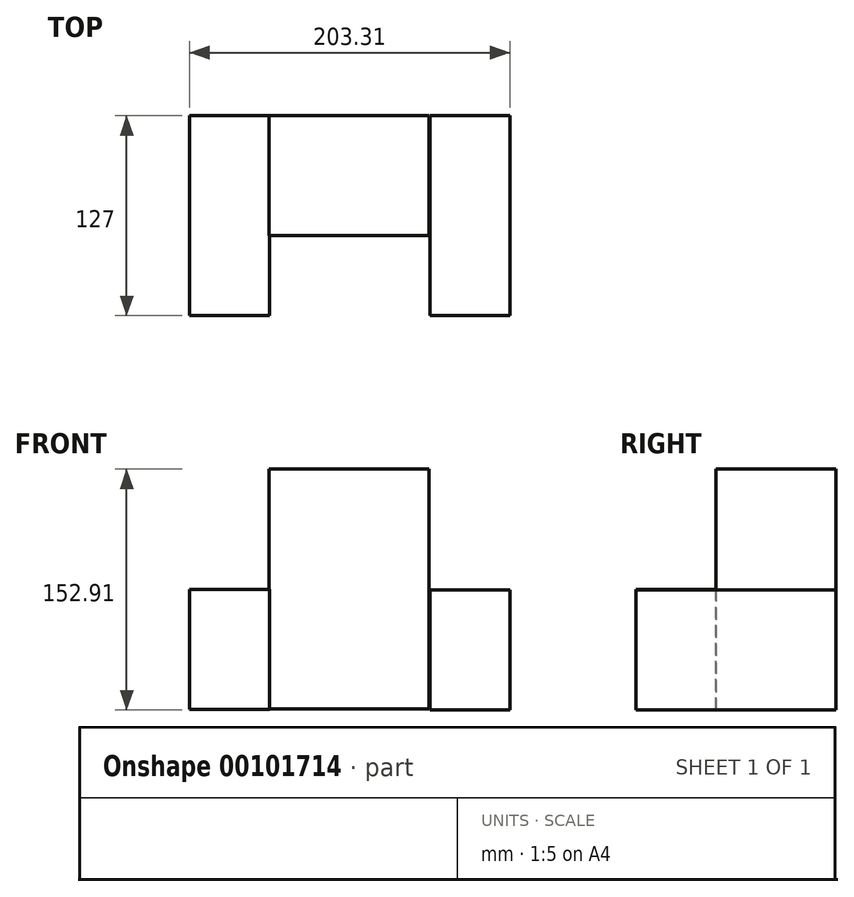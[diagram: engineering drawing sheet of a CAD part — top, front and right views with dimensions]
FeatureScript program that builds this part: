
annotation { "Feature Type Name" : "Feature", "Feature Type Description" : "" }
export const myFeature = defineFeature(function(context is Context, id is Id, definition is map)
    precondition{}
    {
        {
            var Q0;
            Q0=qCreatedBy(makeId("Front.planeOp"),FACE);
            var sketch = newSketch(context, id + "F0", { "sketchPlane" : qUnion([Q0])});
            skLineSegment(sketch, "E0", {"start": v(-108.12, -13.07) * mm, "end": v(-108.12, -89.27) * mm});
            skLineSegment(sketch, "E1", {"start": v(-108.12, -89.27) * mm, "end": v(-57.32, -89.27) * mm});
            skLineSegment(sketch, "E2", {"start": v(-57.32, -89.27) * mm, "end": v(-57.32, -13.07) * mm});
            skLineSegment(sketch, "E3", {"start": v(-57.32, -13.07) * mm, "end": v(-108.12, -13.07) * mm});
            skLineSegment(sketch, "E4", {"start": v(44.4, -13.4) * mm, "end": v(44.4, -89.6) * mm});
            skLineSegment(sketch, "E5", {"start": v(44.4, -89.6) * mm, "end": v(95.2, -89.6) * mm});
            skLineSegment(sketch, "E6", {"start": v(95.2, -89.6) * mm, "end": v(95.2, -13.4) * mm});
            skLineSegment(sketch, "E7", {"start": v(95.2, -13.4) * mm, "end": v(44.4, -13.4) * mm});
            skSolve(sketch);
        }
        {
            var Q0;
            Q0=makeQuery(id+"F0.imprint","IMPRINT",FACE,{"disambiguationData":[TD([[makeQuery(id+"F0.imprint","IMPRINT",EDGE,{"derivedFrom":sQuery(id+"F0.wireOp",EDGE,"E0")}),1.0]])]});
            extrude(context, id + "F1", {"entities" : qUnion([Q0]), "depth" : 127 * mm});
        }
        {
            var Q0;
            Q0 = qSketchRegion(id + "F0", true);
            extrude(context, id + "F2", {"entities" : qUnion([Q0]), "operationType" : NewBodyOperationType.ADD, "depth" : 127 * mm});
        }
        {
            var Q0;
            Q0=qCreatedBy(makeId("Front.planeOp"),FACE);
            var sketch = newSketch(context, id + "F3", { "sketchPlane" : qUnion([Q0])});
            skLineSegment(sketch, "E8", {"start": v(-57.65, -89.1) * mm, "end": v(-57.65, 63.3) * mm});
            skLineSegment(sketch, "E9", {"start": v(-57.65, 63.3) * mm, "end": v(43.95, 63.3) * mm});
            skLineSegment(sketch, "E10", {"start": v(43.95, 63.3) * mm, "end": v(43.95, -89.1) * mm});
            skLineSegment(sketch, "E11", {"start": v(43.95, -89.1) * mm, "end": v(-57.65, -89.1) * mm});
            skSolve(sketch);
        }
        {
            var Q0;
            Q0=makeQuery(id+"F3.imprint","IMPRINT",FACE,{"disambiguationData":[TD([[makeQuery(id+"F3.imprint","IMPRINT",EDGE,{"derivedFrom":sQuery(id+"F3.wireOp",EDGE,"E8")}),-1.0]])]});
            extrude(context, id + "F4", {"entities" : qUnion([Q0]), "depth" : 76.2 * mm});
        }
    });
